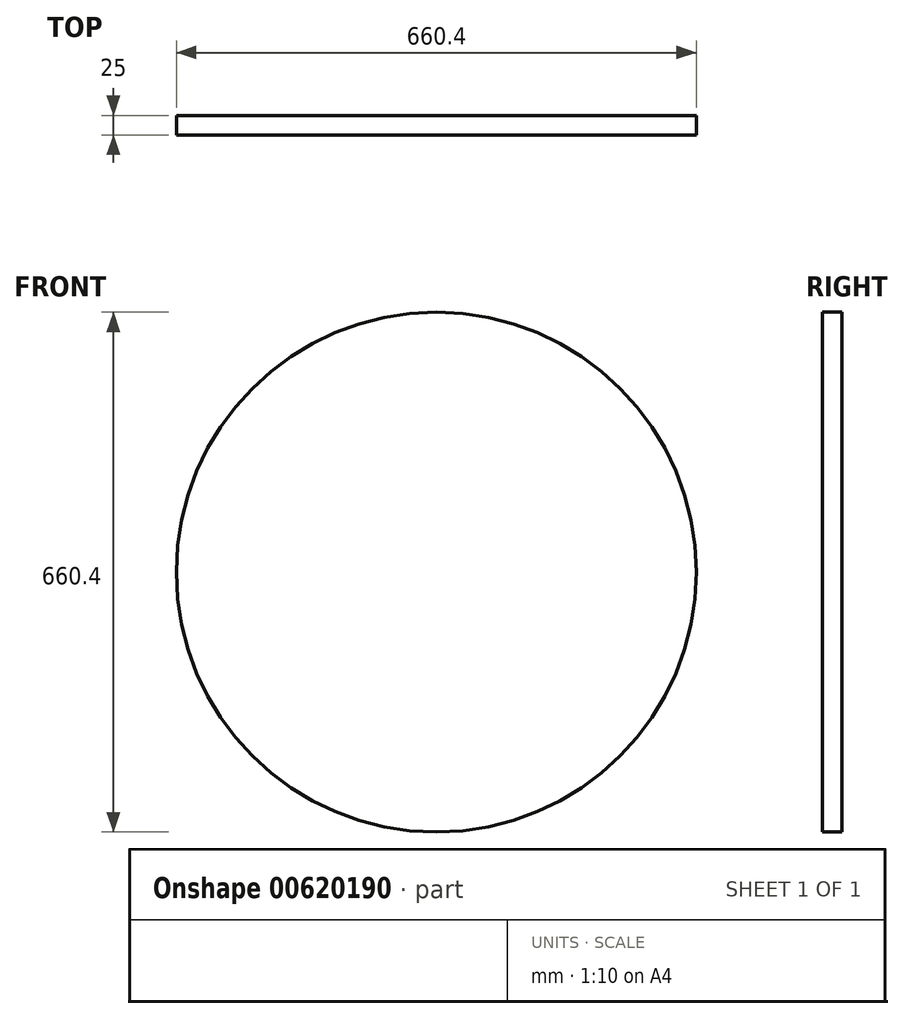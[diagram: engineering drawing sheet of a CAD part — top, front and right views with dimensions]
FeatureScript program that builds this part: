
annotation { "Feature Type Name" : "Feature", "Feature Type Description" : "" }
export const myFeature = defineFeature(function(context is Context, id is Id, definition is map)
    precondition{}
    {
        {
            var Q0;
            Q0=qCreatedBy(makeId("Front.planeOp"),FACE);
            var sketch = newSketch(context, id + "F0", { "sketchPlane" : qUnion([Q0])});
            skCircle(sketch, "E0", {"center": v(0, 0) * mm, "radius": 330.2 * mm});
            skSolve(sketch);
        }
        {
            var Q0;
            Q0=makeQuery(id+"F0.imprint","IMPRINT",FACE,{"disambiguationData":[TD([[makeQuery(id+"F0.imprint","IMPRINT",EDGE,{"derivedFrom":sQuery(id+"F0.wireOp",EDGE,"E0")}),1.0]])]});
            var Q1;
            Q1=sQuery(id+"F0.wireOp",EDGE,"E0");
            extrude(context, id + "F1", {"entities" : qUnion([Q0]), "surfaceEntities" : qUnion([Q1]), "depth" : 25 * mm, "offsetDistance" : 25 * mm});
        }
    });
